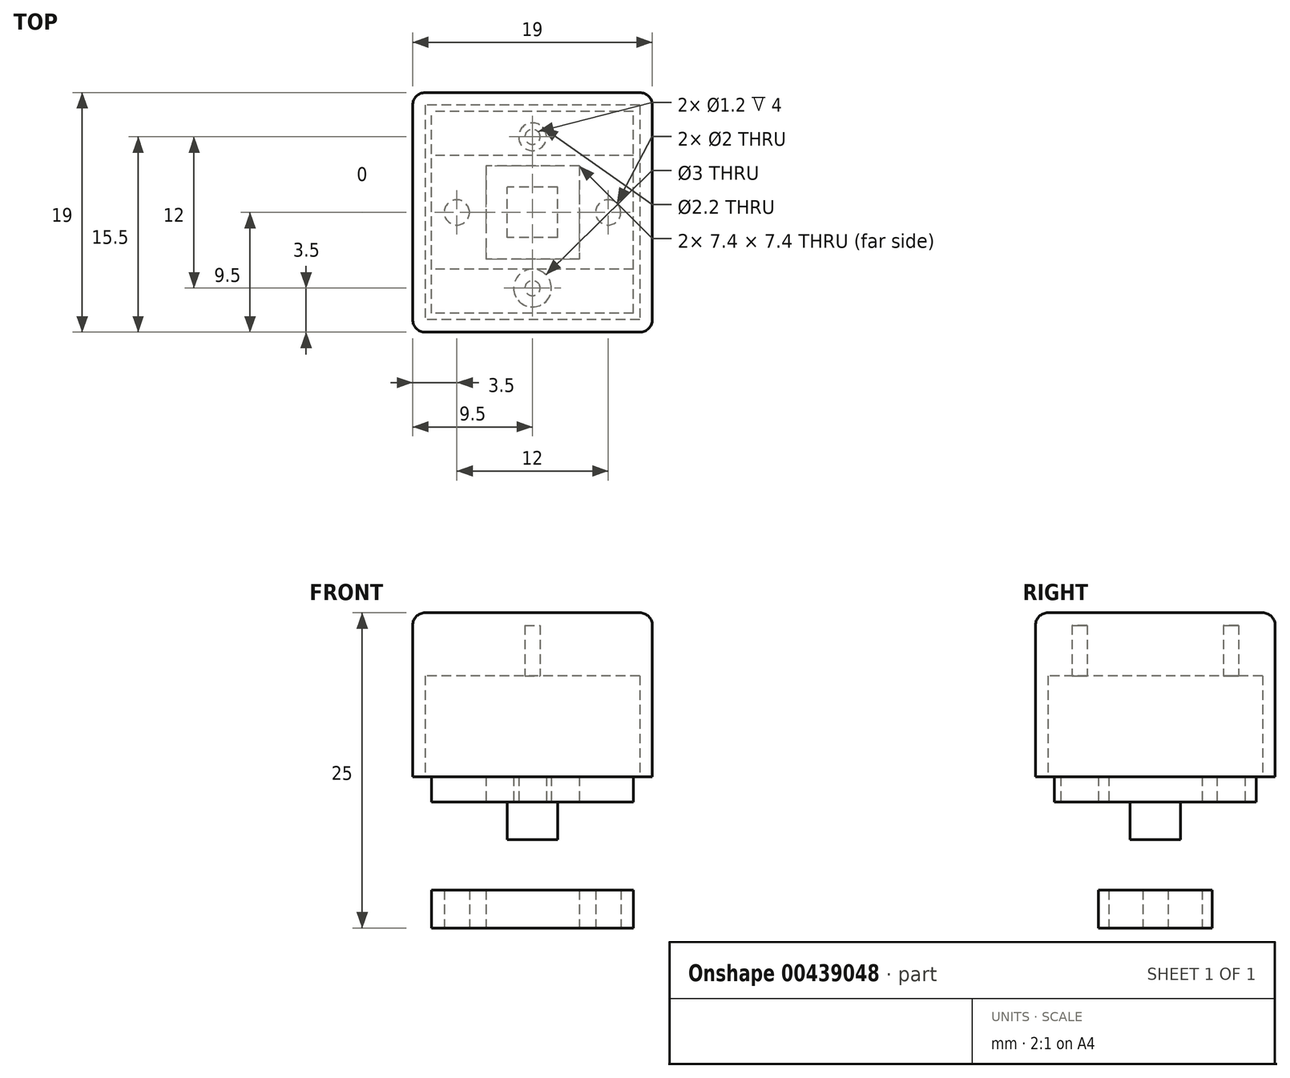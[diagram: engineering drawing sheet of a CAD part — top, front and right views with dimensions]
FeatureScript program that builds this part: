
annotation { "Feature Type Name" : "Feature", "Feature Type Description" : "" }
export const myFeature = defineFeature(function(context is Context, id is Id, definition is map)
    precondition{}
    {
        {
            var Q0;
            Q0=qCreatedBy(makeId("Top.planeOp"),FACE);
            var sketch = newSketch(context, id + "F0", { "sketchPlane" : qUnion([Q0])});
            skLineSegment(sketch, "E0.bottom", {"start": v(3.7, -3.7) * mm, "end": v(-3.7, -3.7) * mm});
            skLineSegment(sketch, "E0.top", {"start": v(3.7, 3.7) * mm, "end": v(-3.7, 3.7) * mm});
            skLineSegment(sketch, "E0.left", {"start": v(3.7, -3.7) * mm, "end": v(3.7, 3.7) * mm});
            skLineSegment(sketch, "E0.right", {"start": v(-3.7, -3.7) * mm, "end": v(-3.7, 3.7) * mm});
            skPoint(sketch, "E0.middle", {"position": v(0, 0) * mm});
            skLineSegment(sketch, "E1.bottom", {"start": v(8, -4.5) * mm, "end": v(-8, -4.5) * mm});
            skLineSegment(sketch, "E1.top", {"start": v(8, 4.5) * mm, "end": v(-8, 4.5) * mm});
            skLineSegment(sketch, "E1.left", {"start": v(8, -4.5) * mm, "end": v(8, 4.5) * mm});
            skLineSegment(sketch, "E1.right", {"start": v(-8, -4.5) * mm, "end": v(-8, 4.5) * mm});
            skCircle(sketch, "E2", {"center": v(-6, 0) * mm, "radius": 1 * mm});
            skCircle(sketch, "E3", {"center": v(6, 0) * mm, "radius": 1 * mm});
            skSolve(sketch);
        }
        {
            var Q0;
            Q0=qSketchRegion(id+"F0",true);
            extrude(context, id + "F1", {"entities" : qUnion([Q0]), "depth" : 3 * mm});
        }
        {
            var Q0;
            Q0=qCreatedBy(makeId("Top.planeOp"),FACE);
            cPlane(context, id + "F2", {"entities" : qUnion([Q0]), "cplaneType" : CPlaneType.OFFSET, "offset" : 10 * mm, "width" : 150 * mm, "height" : 150 * mm});
        }
        {
            var Q0;
            Q0=qCreatedBy(id+"F2.planeOp",FACE);
            var sketch = newSketch(context, id + "F3", { "sketchPlane" : qUnion([Q0])});
            skLineSegment(sketch, "E4.bottom", {"start": v(2, -2) * mm, "end": v(-2, -2) * mm});
            skLineSegment(sketch, "E4.top", {"start": v(2, 2) * mm, "end": v(-2, 2) * mm});
            skLineSegment(sketch, "E4.left", {"start": v(2, -2) * mm, "end": v(2, 2) * mm});
            skLineSegment(sketch, "E4.right", {"start": v(-2, -2) * mm, "end": v(-2, 2) * mm});
            skPoint(sketch, "E4.middle", {"position": v(0, 0) * mm});
            skSolve(sketch);
        }
        {
            var Q0;
            Q0=qSketchRegion(id+"F3",true);
            extrude(context, id + "F4", {"entities" : qUnion([Q0]), "oppositeDirection" : true, "depth" : 3 * mm});
        }
        {
            var Q0;
            Q0=qCreatedBy(id+"F2.planeOp",FACE);
            var sketch = newSketch(context, id + "F5", { "sketchPlane" : qUnion([Q0])});
            skLineSegment(sketch, "E5.bottom", {"start": v(8, -8) * mm, "end": v(-8, -8) * mm});
            skLineSegment(sketch, "E5.top", {"start": v(8, 8) * mm, "end": v(-8, 8) * mm});
            skLineSegment(sketch, "E5.left", {"start": v(8, -8) * mm, "end": v(8, 8) * mm});
            skLineSegment(sketch, "E5.right", {"start": v(-8, -8) * mm, "end": v(-8, 8) * mm});
            skPoint(sketch, "E5.middle", {"position": v(0, 0) * mm});
            skCircle(sketch, "E6", {"center": v(0, -6) * mm, "radius": 1.5 * mm});
            skCircle(sketch, "E7", {"center": v(0, 6) * mm, "radius": 1.1 * mm});
            skSolve(sketch);
        }
        {
            var Q0;
            Q0=qSketchRegion(id+"F5",true);
            extrude(context, id + "F6", {"entities" : qUnion([Q0]), "depth" : 5 * mm});
        }
        {
            var Q0;
            Q0=qCreatedBy(makeId("Top.planeOp"),FACE);
            cPlane(context, id + "F7", {"entities" : qUnion([Q0]), "cplaneType" : CPlaneType.OFFSET, "offset" : 12 * mm, "width" : 150 * mm, "height" : 150 * mm});
        }
        {
            var Q0;
            Q0=qCreatedBy(id+"F7.planeOp",FACE);
            var sketch = newSketch(context, id + "F8", { "sketchPlane" : qUnion([Q0])});
            skLineSegment(sketch, "E8.bottom", {"start": v(9.5, -9.5) * mm, "end": v(-9.5, -9.5) * mm});
            skLineSegment(sketch, "E8.top", {"start": v(9.5, 9.5) * mm, "end": v(-9.5, 9.5) * mm});
            skLineSegment(sketch, "E8.left", {"start": v(9.5, -9.5) * mm, "end": v(9.5, 9.5) * mm});
            skLineSegment(sketch, "E8.right", {"start": v(-9.5, -9.5) * mm, "end": v(-9.5, 9.5) * mm});
            skPoint(sketch, "E8.middle", {"position": v(0, 0) * mm});
            skSolve(sketch);
        }
        {
            var Q0;
            Q0=qSketchRegion(id+"F8",true);
            extrude(context, id + "F9", {"entities" : qUnion([Q0]), "depth" : 13 * mm});
        }
        {
            var Q0;
            Q0=makeQuery(id+"F9.opExtrude","CAP_FACE",FACE,{"disambiguationData":[OSD([sQuery(id+"F8.wireOp",EDGE,"E8.bottom"),sQuery(id+"F8.wireOp",EDGE,"E8.top"),sQuery(id+"F8.wireOp",EDGE,"E8.left"),sQuery(id+"F8.wireOp",EDGE,"E8.right")])],"isStart":true});
            var sketch = newSketch(context, id + "F10", { "sketchPlane" : qUnion([Q0])});
            skLineSegment(sketch, "E9.bottom", {"start": v(8.5, -8.5) * mm, "end": v(-8.5, -8.5) * mm});
            skLineSegment(sketch, "E9.top", {"start": v(8.5, 8.5) * mm, "end": v(-8.5, 8.5) * mm});
            skLineSegment(sketch, "E9.left", {"start": v(8.5, -8.5) * mm, "end": v(8.5, 8.5) * mm});
            skLineSegment(sketch, "E9.right", {"start": v(-8.5, -8.5) * mm, "end": v(-8.5, 8.5) * mm});
            skPoint(sketch, "E9.middle", {"position": v(0, 0) * mm});
            skSolve(sketch);
        }
        {
            var Q0;
            Q0=qSketchRegion(id+"F10",true);
            extrude(context, id + "F11", {"entities" : qUnion([Q0]), "operationType" : NewBodyOperationType.REMOVE, "oppositeDirection" : true, "depth" : 8 * mm});
        }
        {
            var Q0;
            Q0=makeQuery(id+"F11.boolean.opBoolean","COPY",FACE,{"derivedFrom":makeQuery(id+"F11.opExtrude","CAP_FACE",FACE,{"disambiguationData":[OSD([sQuery(id+"F10.wireOp",EDGE,"E9.bottom"),sQuery(id+"F10.wireOp",EDGE,"E9.top"),sQuery(id+"F10.wireOp",EDGE,"E9.left"),sQuery(id+"F10.wireOp",EDGE,"E9.right")])],"isStart":false})});
            var sketch = newSketch(context, id + "F12", { "sketchPlane" : qUnion([Q0])});
            skCircle(sketch, "E10", {"center": v(0, 6) * mm, "radius": 0.6 * mm});
            skCircle(sketch, "E11", {"center": v(0, -6) * mm, "radius": 0.6 * mm});
            skSolve(sketch);
        }
        {
            var Q0;
            Q0=qSketchRegion(id+"F12",true);
            extrude(context, id + "F13", {"entities" : qUnion([Q0]), "operationType" : NewBodyOperationType.REMOVE, "oppositeDirection" : true, "depth" : 4 * mm});
        }
        {
            var Q0;
            Q0=makeQuery(id+"F9.opExtrude","SWEPT_EDGE",EDGE,{"disambiguationData":[OSD([sQuery(id+"F8.wireOp",EDGE,"E8.bottom"),sQuery(id+"F8.wireOp",EDGE,"E8.right")])]});
            var Q1;
            Q1=makeQuery(id+"F9.opExtrude","SWEPT_EDGE",EDGE,{"disambiguationData":[OSD([sQuery(id+"F8.wireOp",EDGE,"E8.bottom"),sQuery(id+"F8.wireOp",EDGE,"E8.left")])]});
            var Q2;
            Q2=makeQuery(id+"F9.opExtrude","SWEPT_EDGE",EDGE,{"disambiguationData":[OSD([sQuery(id+"F8.wireOp",EDGE,"E8.top"),sQuery(id+"F8.wireOp",EDGE,"E8.right")])]});
            var Q3;
            Q3=makeQuery(id+"F9.opExtrude","SWEPT_EDGE",EDGE,{"disambiguationData":[OSD([sQuery(id+"F8.wireOp",EDGE,"E8.top"),sQuery(id+"F8.wireOp",EDGE,"E8.left")])]});
            var Q4;
            Q4=makeQuery(id+"F9.opExtrude","CAP_FACE",FACE,{"disambiguationData":[OSD([sQuery(id+"F8.wireOp",EDGE,"E8.bottom"),sQuery(id+"F8.wireOp",EDGE,"E8.top"),sQuery(id+"F8.wireOp",EDGE,"E8.left"),sQuery(id+"F8.wireOp",EDGE,"E8.right")])],"isStart":false});
            fillet(context, id + "F14", {"entities" : qUnion([Q0, Q1, Q2, Q3, Q4]), "radius" : 1 * mm, "tangentPropagation" : true, "allowEdgeOverflow" : false});
        }
        {
            var Q0;
            Q0=makeQuery(id+"F6.opExtrude","CAP_FACE",FACE,{"disambiguationData":[OSD([sQuery(id+"F5.wireOp",EDGE,"E5.bottom"),sQuery(id+"F5.wireOp",EDGE,"E5.top"),sQuery(id+"F5.wireOp",EDGE,"E5.left"),sQuery(id+"F5.wireOp",EDGE,"E5.right"),sQuery(id+"F5.wireOp",EDGE,"E6"),sQuery(id+"F5.wireOp",EDGE,"E7")])],"isStart":true});
            var sketch = newSketch(context, id + "F15", { "sketchPlane" : qUnion([Q0])});
            skLineSegment(sketch, "E12.bottom", {"start": v(3.7, -3.7) * mm, "end": v(-3.7, -3.7) * mm});
            skLineSegment(sketch, "E12.top", {"start": v(3.7, 3.7) * mm, "end": v(-3.7, 3.7) * mm});
            skLineSegment(sketch, "E12.left", {"start": v(3.7, -3.7) * mm, "end": v(3.7, 3.7) * mm});
            skLineSegment(sketch, "E12.right", {"start": v(-3.7, -3.7) * mm, "end": v(-3.7, 3.7) * mm});
            skPoint(sketch, "E12.middle", {"position": v(0, 0) * mm});
            skSolve(sketch);
        }
        {
            var Q0;
            Q0=qSketchRegion(id+"F15",true);
            extrude(context, id + "F16", {"entities" : qUnion([Q0]), "operationType" : NewBodyOperationType.REMOVE, "oppositeDirection" : true, "depth" : 3.5 * mm});
        }
    });
